# Revit family: PTT, PSS, 189, 1815, 2115, 2415, 1818, 2118, 2418
name_source: partatom
category: Windows
revit_build: Autodesk Revit LT 2016 (Build: 20150220_1215(x64)
units: mm (PartAtom-declared; Revit-internal decimal feet)

## family parameters
Always vertical = Yes
Cut with Voids When Loaded = No
Host = Wall
OmniClass Number = 23.30.20.00
OmniClass Title = Windows
Room Calculation Point = No
Shared = No

## types (7) — shared parameters
Aluminium anodized = Aluminium
Centre vert mullion = 610 mm  [stored 2.00131 ft]
Default Sill Height = 914 mm
Glazing = Glass
Manufacturer = Robmeg
Plaster = 5 mm  [stored 0.0164042 ft]
Rough Height = 1219 mm
URL = http://www.robmeg.co.za
Wall Closure = By host

## per-type parameters (varying)
| type | Bottom fixed glass width | Bottom mullion height | Centre fixed glass width | Description | Height | Model | Side hung | Top hung | Width |
| PTT Type -189 | 4 mm  [stored 0.0131234 ft] | 300 mm | 4 mm  [stored 0.0131234 ft] | Anodized Aluminium | 910 mm | PTT 189 | No | Yes | 1810 mm  [stored 5.93832 ft] |
| PSS Type- 1815 | 4 mm  [stored 0.0131234 ft] | 300 mm | 4 mm  [stored 0.0131234 ft] | Anodized Aluminium | 1510 mm  [stored 4.95407 ft] | PSS 1815 | Yes | No | 1810 mm  [stored 5.93832 ft] |
| PSS Type- 2115 | 4 mm  [stored 0.0131234 ft] | 300 mm | 4 mm  [stored 0.0131234 ft] | Anodized Aluminium | 1510 mm  [stored 4.95407 ft] | PSS 2115 | Yes | No | 2110 mm  [stored 6.92257 ft] |
| PSS Type- 2415 | 4 mm  [stored 0.0131234 ft] | 300 mm | 4 mm  [stored 0.0131234 ft] | Anodized Aluminium | 1510 mm  [stored 4.95407 ft] | PSS 2415 | Yes | No | 2410 mm  [stored 7.90682 ft] |
| PSS Type- 1818 | 6 mm  [stored 0.019685 ft] | 605 mm  [stored 1.98491 ft] | 6 mm  [stored 0.019685 ft] | Anodized Aluminium | 1810 mm  [stored 5.93832 ft] | PSS 1818 | Yes | No | 1810 mm  [stored 5.93832 ft] |
| PSS Type- 2118 | 6 mm  [stored 0.019685 ft] | 605 mm  [stored 1.98491 ft] | 6 mm  [stored 0.019685 ft] | Anodized Aluminium | 1810 mm  [stored 5.93832 ft] | PSS 2118 | Yes | No | 2110 mm  [stored 6.92257 ft] |
| PSS Type- 2418 | 6 mm  [stored 0.019685 ft] | 605 mm  [stored 1.98491 ft] | 6 mm  [stored 0.019685 ft] | Anodized aluminium | 1810 mm  [stored 5.93832 ft] | PSS 2418 | Yes | No | 2410 mm  [stored 7.90682 ft] |

note: [stored X ft] marks values corroborated as IEEE doubles in the binary element streams (Revit-internal decimal feet)

## geometry (parser evidence)
native form markers: Sweep x3
no freeform markers — native parametric forms only
